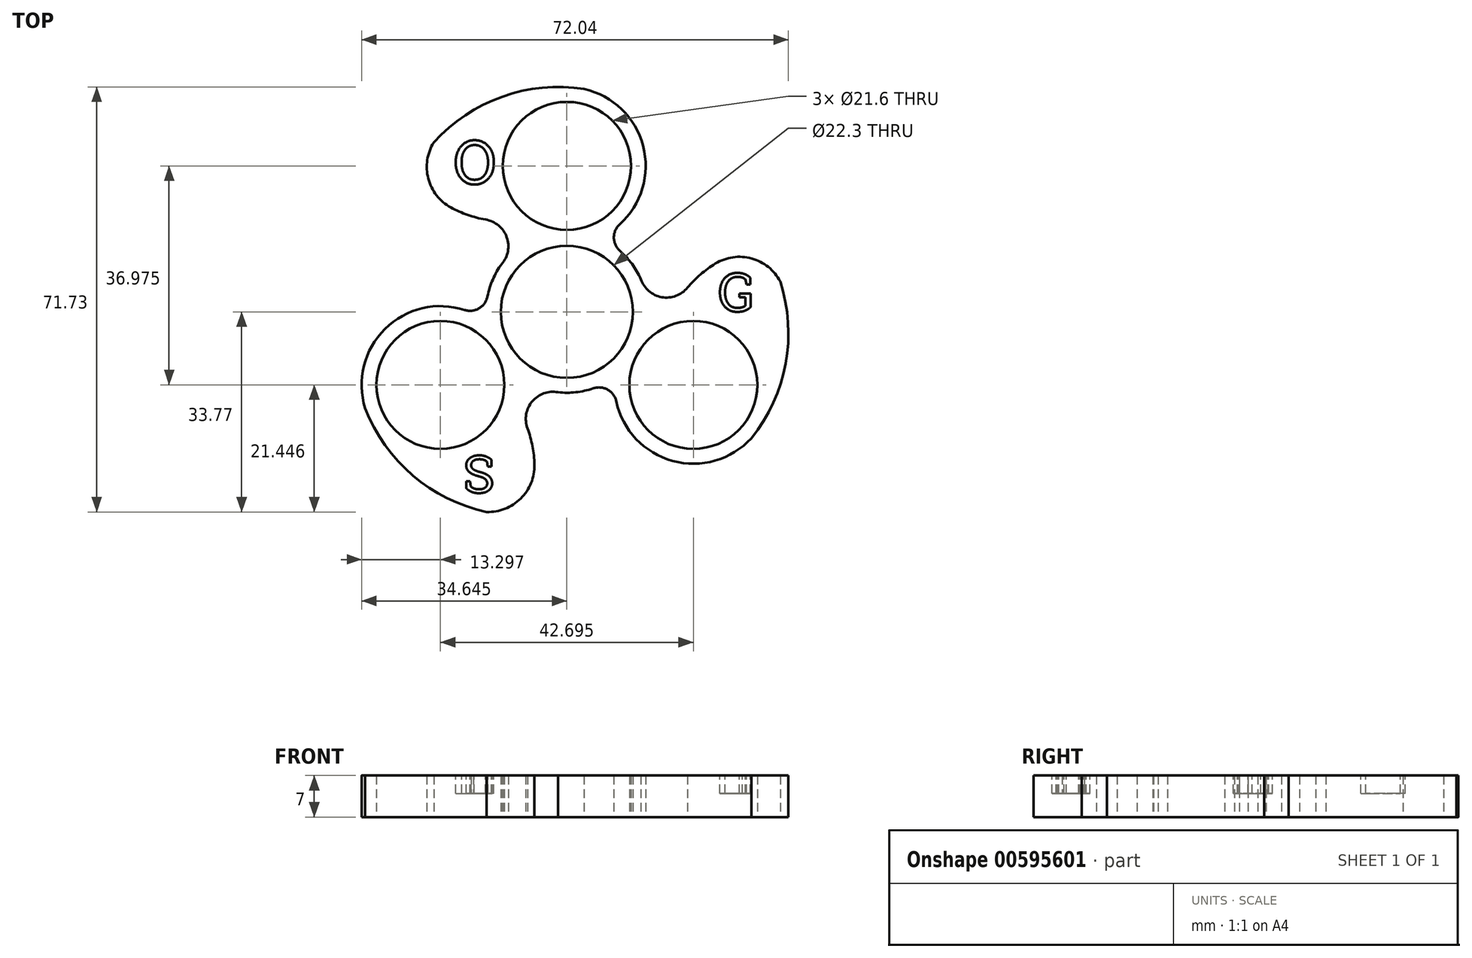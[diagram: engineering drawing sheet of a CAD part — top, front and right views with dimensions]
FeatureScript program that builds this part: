
annotation { "Feature Type Name" : "Feature", "Feature Type Description" : "" }
export const myFeature = defineFeature(function(context is Context, id is Id, definition is map)
    precondition{}
    {
        {
            var Q0;
            Q0=qCreatedBy(makeId("Top.planeOp"),FACE);
            var sketch = newSketch(context, id + "F0", { "sketchPlane" : qUnion([Q0])});
            skCircle(sketch, "E0", {"center": v(-23.02, -6.58) * mm, "radius": 11.15 * mm});
            skLineSegment(sketch, "E1", {"start": v(-23.02, -6.58) * mm, "end": v(-23.02, 18.07) * mm});
            skCircle(sketch, "E2", {"center": v(-23.02, 18.07) * mm, "radius": 10.8 * mm});
            skCircle(sketch, "E3.1.0", {"center": v(-44.36, -18.9) * mm, "radius": 10.8 * mm});
            skCircle(sketch, "E3.2.0", {"center": v(-1.67, -18.9) * mm, "radius": 10.8 * mm});
            skArc(sketch, "E4.0", {"start": v(-14.1, 8.2) * mm, "mid": v(-10.15, 21.45) * mm, "end": v(-20.1, 31.05) * mm});
            skArc(sketch, "E5.0", {"start": v(-34.02, 1.5) * mm, "mid": v(-35.52, -1.1) * mm, "end": v(-36.41, -3.97) * mm});
            skArc(sketch, "E6.filletArc", {"start": v(-14.1, 8.2) * mm, "mid": v(-15.08, 5.95) * mm, "end": v(-14.05, 3.72) * mm});
            skArc(sketch, "E7", {"start": v(-34.02, 1.5) * mm, "mid": v(-33.17, 6.04) * mm, "end": v(-36.73, 9) * mm});
            skArc(sketch, "E8", {"start": v(-45.49, 22.03) * mm, "mid": v(-46.41, 15.92) * mm, "end": v(-42.61, 11.05) * mm});
            skArc(sketch, "E9", {"start": v(-20.1, 31.05) * mm, "mid": v(-33.93, 29.75) * mm, "end": v(-45.49, 22.03) * mm});
            skArc(sketch, "E10", {"start": v(-42.61, 11.05) * mm, "mid": v(-39.75, 9.8) * mm, "end": v(-36.73, 9) * mm});
            skArc(sketch, "E11.1.0", {"start": v(-36.55, -40.34) * mm, "mid": v(-30.8, -38.1) * mm, "end": v(-28.48, -32.37) * mm});
            skArc(sketch, "E11.1.1", {"start": v(-28.48, -32.37) * mm, "mid": v(-28.83, -29.26) * mm, "end": v(-29.65, -26.25) * mm});
            skArc(sketch, "E11.1.2", {"start": v(-24.5, -20.15) * mm, "mid": v(-28.87, -21.69) * mm, "end": v(-29.65, -26.25) * mm});
            skArc(sketch, "E11.1.3", {"start": v(-40.28, -6.25) * mm, "mid": v(-53.72, -9.45) * mm, "end": v(-57.06, -22.86) * mm});
            skArc(sketch, "E11.1.4", {"start": v(-40.28, -6.25) * mm, "mid": v(-37.83, -5.98) * mm, "end": v(-36.41, -3.97) * mm});
            skArc(sketch, "E11.1.5", {"start": v(-57.06, -22.86) * mm, "mid": v(-49.02, -34.2) * mm, "end": v(-36.55, -40.34) * mm});
            skArc(sketch, "E11.2.0", {"start": v(13, -1.42) * mm, "mid": v(8.17, 2.43) * mm, "end": v(2.05, 1.58) * mm});
            skArc(sketch, "E11.2.1", {"start": v(2.05, 1.58) * mm, "mid": v(-0.47, -0.27) * mm, "end": v(-2.66, -2.5) * mm});
            skArc(sketch, "E11.2.2", {"start": v(-10.52, -1.08) * mm, "mid": v(-7, -4.1) * mm, "end": v(-2.66, -2.5) * mm});
            skArc(sketch, "E11.2.3", {"start": v(-14.67, -21.7) * mm, "mid": v(-5.17, -31.73) * mm, "end": v(8.11, -27.92) * mm});
            skArc(sketch, "E11.2.4", {"start": v(-14.67, -21.7) * mm, "mid": v(-16.13, -19.71) * mm, "end": v(-18.58, -19.49) * mm});
            skArc(sketch, "E11.2.5", {"start": v(8.11, -27.92) * mm, "mid": v(13.9, -15.29) * mm, "end": v(13, -1.42) * mm});
            skArc(sketch, "E12.trimOffspring", {"start": v(-25.06, -20.08) * mm, "mid": v(-21.78, -20.17) * mm, "end": v(-18.58, -19.49) * mm});
            skArc(sketch, "E13.trimOffspring", {"start": v(-10.3, -1.6) * mm, "mid": v(-11.86, 1.28) * mm, "end": v(-14.05, 3.72) * mm});
            skSolve(sketch);
        }
        {
            var Q0;
            Q0=makeQuery(id+"F0.imprint","IMPRINT",FACE,{"disambiguationData":[TD([[makeQuery(id+"F0.imprint","IMPRINT",EDGE,{"derivedFrom":sQuery(id+"F0.wireOp",EDGE,"E0")}),-1.0]])]});
            extrude(context, id + "F1", {"entities" : qUnion([Q0]), "depth" : 7 * mm, "offsetDistance" : 25 * mm});
        }
        {
            var Q0;
            Q0=makeQuery(id+"F1.opExtrude","CAP_FACE",FACE,{"disambiguationData":[OSD([sQuery(id+"F0.wireOp",EDGE,"E0"),sQuery(id+"F0.wireOp",EDGE,"E2"),sQuery(id+"F0.wireOp",EDGE,"E3.1.0"),sQuery(id+"F0.wireOp",EDGE,"E3.2.0"),sQuery(id+"F0.wireOp",EDGE,"E4.0"),sQuery(id+"F0.wireOp",EDGE,"E5.0"),sQuery(id+"F0.wireOp",EDGE,"E6.filletArc"),sQuery(id+"F0.wireOp",EDGE,"E7"),sQuery(id+"F0.wireOp",EDGE,"E8"),sQuery(id+"F0.wireOp",EDGE,"E9"),sQuery(id+"F0.wireOp",EDGE,"E10"),sQuery(id+"F0.wireOp",EDGE,"E11.1.0"),sQuery(id+"F0.wireOp",EDGE,"E11.1.1"),sQuery(id+"F0.wireOp",EDGE,"E11.1.2"),sQuery(id+"F0.wireOp",EDGE,"E11.1.3"),sQuery(id+"F0.wireOp",EDGE,"E11.1.4"),sQuery(id+"F0.wireOp",EDGE,"E11.1.5"),sQuery(id+"F0.wireOp",EDGE,"E11.2.0"),sQuery(id+"F0.wireOp",EDGE,"E11.2.1"),sQuery(id+"F0.wireOp",EDGE,"E11.2.2"),sQuery(id+"F0.wireOp",EDGE,"E11.2.3"),sQuery(id+"F0.wireOp",EDGE,"E11.2.4"),sQuery(id+"F0.wireOp",EDGE,"E11.2.5"),sQuery(id+"F0.wireOp",EDGE,"E12.trimOffspring"),sQuery(id+"F0.wireOp",EDGE,"E13.trimOffspring")])],"isStart":false});
            var sketch = newSketch(context, id + "F2", { "sketchPlane" : qUnion([Q0])});
            skText(sketch, "E14", { "text": "O\n", "fontName": "RobotoSlab-Regular.ttf"});
            skText(sketch, "E15", { "text": "G", "fontName": "RobotoSlab-Regular.ttf"});
            skText(sketch, "E16", { "text": "S", "fontName": "RobotoSlab-Regular.ttf"});
            const initialGuessF2  = {"E14": [-0.04217, 0.01502, 1, 0, 0.00737], "E15": [0.00258, -0.00649, 1, 0, 0.00649], "E16": [-0.04054, -0.0371, 1, 0, 0.0063]};
            skSetInitialGuess(sketch, initialGuessF2);
            skSolve(sketch);
        }
        {
            var Q0;
            Q0 = qSketchRegion(id + "F2", true);
            extrude(context, id + "F3", {"entities" : qUnion([Q0]), "operationType" : NewBodyOperationType.REMOVE, "oppositeDirection" : true, "depth" : 3 * mm, "offsetDistance" : 25 * mm});
        }
    });
